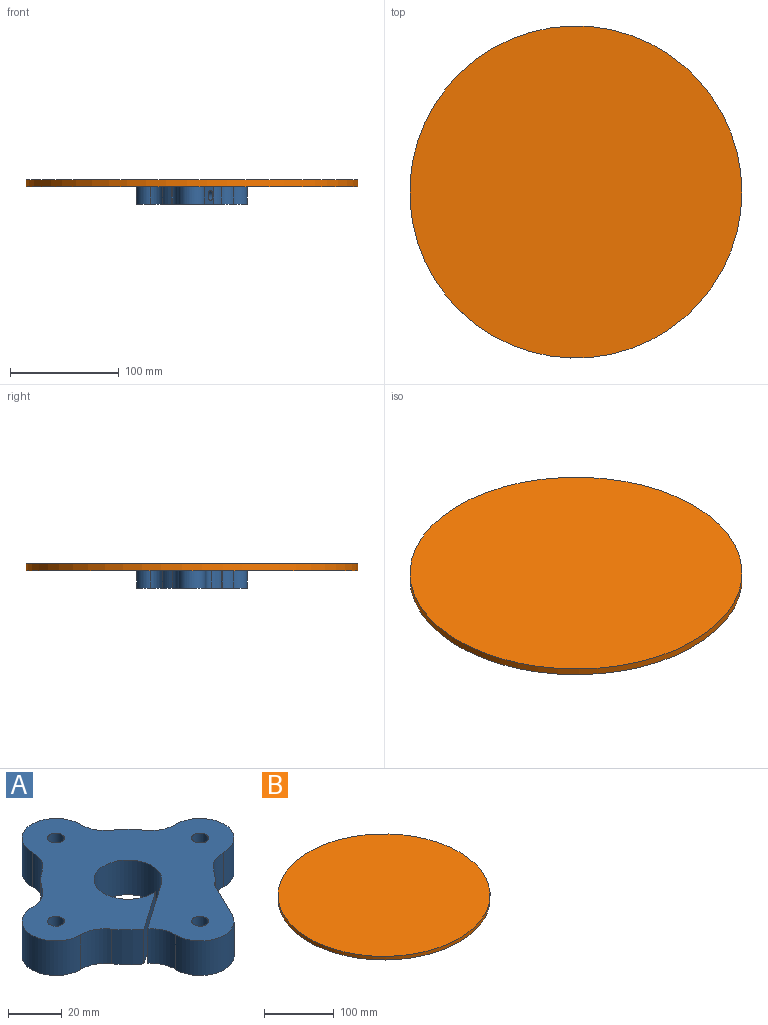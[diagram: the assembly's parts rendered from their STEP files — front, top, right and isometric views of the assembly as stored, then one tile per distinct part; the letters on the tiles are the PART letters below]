
ASSEMBLY  parts=2 mates=1
PART A: 30 faces, bbox 101.6x101.6x15.9 mm
  f0: cylinder r=12.7mm len=15.88mm, axis (0,0,-1), area 183.6mm2, adj f14,f20,f21,f23
  f1: cylinder r=32.61mm len=15.88mm, axis (0,0,-1), area 157.7mm2, adj f2,f20,f21,f22
  f2: cylinder r=12.7mm len=15.88mm, axis (0,0,-1), area 201.3mm2, adj f1,f3,f20,f21
  f3: cylinder r=12.7mm len=25.4mm, axis (0,0,-1), area 642.5mm2, adj f2,f4,f20,f21
  f4: cylinder r=12.7mm len=15.88mm, axis (0,0,-1), area 201.3mm2, adj f3,f5,f20,f21
  f5: cylinder r=32.61mm len=15.88mm, axis (0,0,-1), area 197.2mm2, adj f4,f6,f20,f21
  f6: cylinder r=12.7mm len=15.88mm, axis (0,0,-1), area 201.3mm2, adj f5,f7,f20,f21
  f7: cylinder r=12.7mm len=25.4mm, axis (0,0,-1), area 642.5mm2, adj f6,f8,f20,f21
  f8: cylinder r=12.7mm len=15.88mm, axis (0,0,-1), area 201.3mm2, adj f7,f9,f20,f21
  f9: cylinder r=32.61mm len=15.88mm, axis (0,0,-1), area 197.2mm2, adj f8,f10,f20,f21
  f10: cylinder r=12.7mm len=15.88mm, axis (0,0,-1), area 201.3mm2, adj f9,f11,f20,f21
  f11: cylinder r=12.7mm len=25.4mm, axis (0,0,-1), area 642.5mm2, adj f10,f12,f20,f21
  f12: cylinder r=12.7mm len=15.88mm, axis (0,0,-1), area 201.3mm2, adj f11,f13,f20,f21
  f13: cylinder r=32.61mm len=15.88mm, axis (0,0,-1), area 193.6mm2, adj f12,f20,f21,f24
  f14: cylinder r=12.7mm len=24.11mm, axis (0,0,-1), area 546.2mm2, adj f0,f20,f21,f22
  f15: cylinder r=3.17mm len=15.88mm, axis (0,0,-1), area 316.7mm2, adj f20,f21
  f16: cylinder r=3.17mm len=15.88mm, axis (0,0,-1), area 316.7mm2, adj f20,f21
  f17: cylinder r=3.17mm len=15.88mm, axis (0,0,-1), area 316.7mm2, adj f20,f21
  f18: cylinder r=12.7mm len=25.4mm, axis (0,0,-1), area 1175.8mm2, adj f20,f21,f23,f24
  f19: cylinder r=3.17mm len=15.88mm, axis (0,0,-1), area 316.7mm2, adj f20,f21
  f20: plane 101.6x101.6mm, normal (0,0,1), area 4429.3mm2, adj f0,f1,f2,f3,f4,f5,f6,f7
  f21: plane 101.6x101.6mm, normal (0,0,-1), area 4429.3mm2, adj f0,f1,f2,f3,f4,f5,f6,f7
  f22: plane 18.15x15.88mm, normal (0.9,-0.44,0), area 249.4mm2, adj f1,f14,f20,f21,f25
  f23: plane 24.66x17.27mm, normal (-0.57,0.82,0), area 441.8mm2, adj f0,f18,f20,f21,f27
  f24: plane 20.48x15.88mm, normal (0.57,-0.82,0), area 373.8mm2, adj f13,f18,f20,f21,f28
  f25: cylinder r=4.76mm len=11.9mm, axis (0.9,-0.44,0), area 228mm2, adj f22,f26
  f26: plane 9.53x8.56mm, normal (0.9,-0.44,0), area 39.6mm2, adj f25,f27
  f27: cylinder r=3.17mm len=21.43mm, axis (0.9,-0.44,0), area 378.4mm2, adj f23,f26
  f28: cylinder r=2.54mm len=31.47mm, axis (0.9,-0.44,0), area 497mm2, adj f24,f29
  f29: plane 5.08x4.56mm, normal (0.9,-0.44,0), area 20.3mm2, adj f28
PART B: 3 faces, bbox 304.8x304.8x6.4 mm
  f0: cylinder r=152.4mm len=304.8mm, axis (0,0,-1), area 6080.5mm2, adj f1,f2
  f1: plane 304.8x304.8mm, normal (0,0,1), area 72965.9mm2, adj f0
  f2: plane 304.8x304.8mm, normal (0,0,-1), area 72965.9mm2, adj f0
PLACE A at identity fixed
PLACE B rot(axis=(1,0,0),180deg) t=(-3.14,-5.68,38.1)mm
MATE fastened B.f0 <-> A.f18  axis (0,0,-1) through (0,0,15.88)mm
